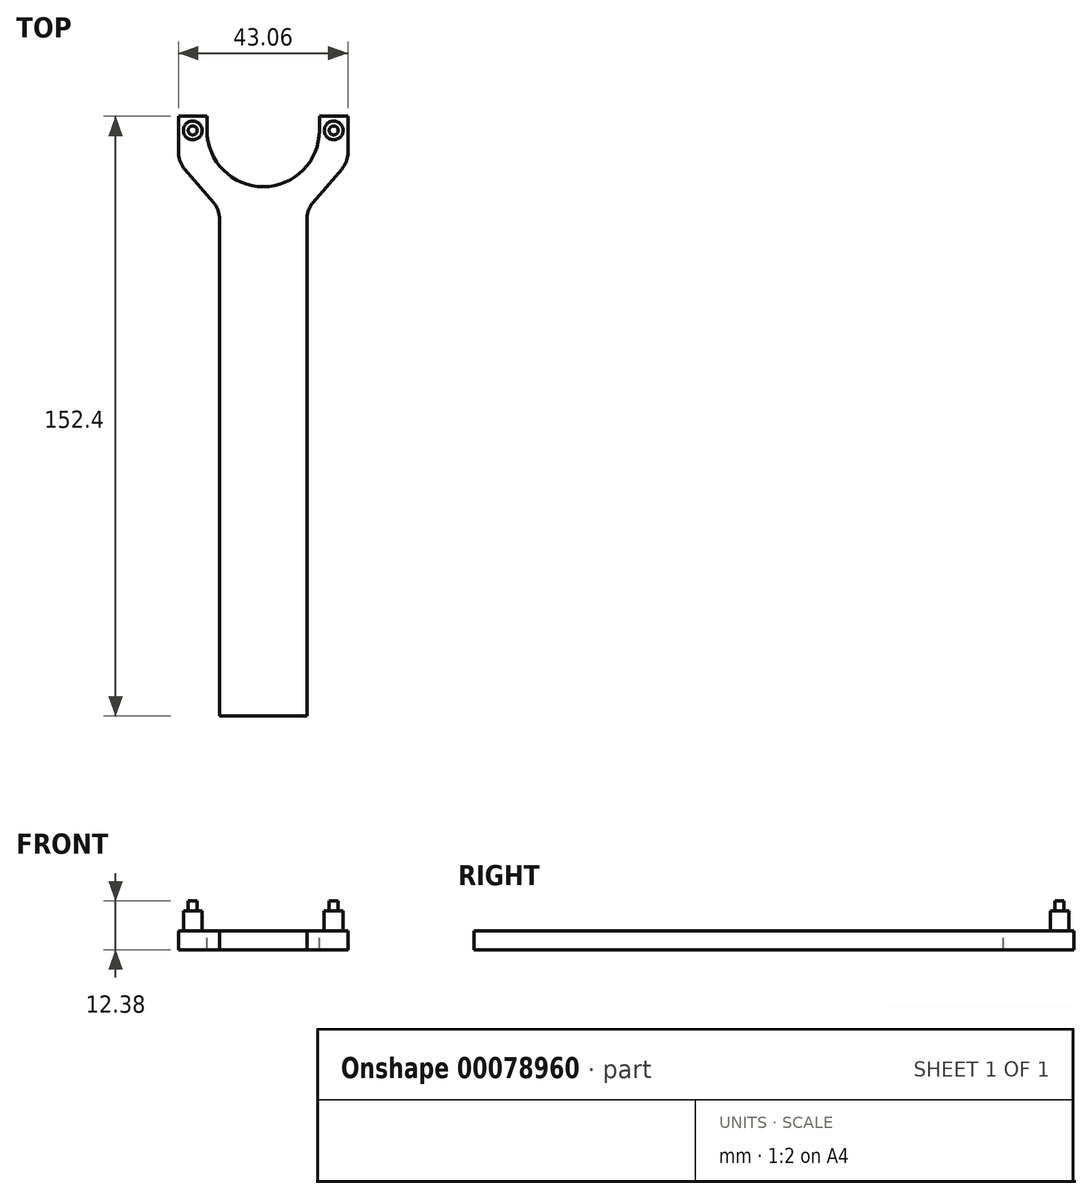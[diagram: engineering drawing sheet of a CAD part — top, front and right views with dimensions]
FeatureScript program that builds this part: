
annotation { "Feature Type Name" : "Feature", "Feature Type Description" : "" }
export const myFeature = defineFeature(function(context is Context, id is Id, definition is map)
    precondition{}
    {
        {
            var Q0;
            Q0=qCreatedBy(makeId("Top.planeOp"),FACE);
            var sketch = newSketch(context, id + "F0", { "sketchPlane" : qUnion([Q0])});
            skLineSegment(sketch, "E0.rect.bottom", {"start": v(21.53, 76.2) * mm, "end": v(14.29, 76.2) * mm});
            skLineSegment(sketch, "E0.rect.left", {"start": v(21.53, 76.2) * mm, "end": v(21.53, 64.6) * mm});
            skLineSegment(sketch, "E0.rect.right", {"start": v(-21.53, 76.2) * mm, "end": v(-21.53, 64.6) * mm});
            skPoint(sketch, "E0.rect.middle", {"position": v(0, 0) * mm});
            skCircle(sketch, "E1", {"center": v(17.9, 72.58) * mm, "radius": 2.38 * mm});
            skCircle(sketch, "E2", {"center": v(-17.9, 72.58) * mm, "radius": 2.38 * mm});
            skLineSegment(sketch, "E3", {"start": v(17.9, 72.58) * mm, "end": v(21.53, 72.58) * mm, "construction": true});
            skLineSegment(sketch, "E4", {"start": v(-17.9, 72.58) * mm, "end": v(-21.53, 72.58) * mm, "construction": true});
            skLineSegment(sketch, "E5", {"start": v(17.9, 72.58) * mm, "end": v(17.9, 76.2) * mm, "construction": true});
            skArc(sketch, "E6", {"start": v(-14.29, 72.58) * mm, "mid": v(0, 58.3) * mm, "end": v(14.29, 72.58) * mm});
            skLineSegment(sketch, "E7", {"start": v(-14.29, 72.58) * mm, "end": v(-14.29, 76.2) * mm});
            skLineSegment(sketch, "E8", {"start": v(14.29, 72.58) * mm, "end": v(14.29, 76.2) * mm});
            skLineSegment(sketch, "E9.trimOffspring", {"start": v(-14.29, 76.2) * mm, "end": v(-21.53, 76.2) * mm});
            skLineSegment(sketch, "E10", {"start": v(17.9, 72.58) * mm, "end": v(14.29, 72.58) * mm, "construction": true});
            skLineSegment(sketch, "E11", {"start": v(-17.9, 72.58) * mm, "end": v(-14.29, 72.58) * mm, "construction": true});
            skLineSegment(sketch, "E12.rect.left", {"start": v(14.29, 76.2) * mm, "end": v(14.29, 72.58) * mm});
            skLineSegment(sketch, "E12.rect.right", {"start": v(-14.29, 76.2) * mm, "end": v(-14.29, 72.58) * mm});
            skCircle(sketch, "E13", {"center": v(0, 72.58) * mm, "radius": 21.53 * mm, "construction": true});
            skLineSegment(sketch, "E14", {"start": v(0, 58.3) * mm, "end": v(0, 51.05) * mm, "construction": true});
            skLineSegment(sketch, "E15", {"start": v(21.53, 64.6) * mm, "end": v(11.11, 52.49) * mm});
            skPoint(sketch, "E16", {"position": v(16.32, 58.54) * mm});
            skLineSegment(sketch, "E17", {"start": v(-21.53, 64.6) * mm, "end": v(-11.11, 52.49) * mm});
            skPoint(sketch, "E18.orphan", {"position": v(-21.53, -76.2) * mm});
            skPoint(sketch, "E19.orphan", {"position": v(21.53, -76.2) * mm});
            skLineSegment(sketch, "E20", {"start": v(-11.11, 52.49) * mm, "end": v(-11.11, -76.2) * mm});
            skLineSegment(sketch, "E21", {"start": v(-11.11, -76.2) * mm, "end": v(11.11, -76.2) * mm});
            skLineSegment(sketch, "E22", {"start": v(11.11, -76.2) * mm, "end": v(11.11, 52.49) * mm});
            skPoint(sketch, "E23", {"position": v(-16.32, 58.54) * mm});
            skCircle(sketch, "E24", {"center": v(-17.9, 72.58) * mm, "radius": 1.14 * mm});
            skCircle(sketch, "E25", {"center": v(17.9, 72.58) * mm, "radius": 1.14 * mm});
            skSolve(sketch);
        }
        {
            var Q0;
            Q0=makeQuery(id+"F0.imprint","IMPRINT",FACE,{"disambiguationData":[TD([[makeQuery(id+"F0.imprint","IMPRINT",EDGE,{"derivedFrom":sQuery(id+"F0.wireOp",EDGE,"E0.rect.bottom")}),1.0]])]});
            var Q1;
            Q1=makeQuery(id+"F0.imprint","IMPRINT",FACE,{"disambiguationData":[TD([[makeQuery(id+"F0.imprint","IMPRINT",EDGE,{"derivedFrom":sQuery(id+"F0.wireOp",EDGE,"E2")}),1.0]])]});
            var Q2;
            Q2=makeQuery(id+"F0.imprint","IMPRINT",FACE,{"disambiguationData":[TD([[makeQuery(id+"F0.imprint","IMPRINT",EDGE,{"derivedFrom":sQuery(id+"F0.wireOp",EDGE,"E1")}),1.0]])]});
            var Q3;
            Q3=makeQuery(id+"F0.imprint","IMPRINT",FACE,{"disambiguationData":[TD([[makeQuery(id+"F0.imprint","IMPRINT",EDGE,{"derivedFrom":sQuery(id+"F0.wireOp",EDGE,"E24")}),1.0]])]});
            var Q4;
            Q4=makeQuery(id+"F0.imprint","IMPRINT",FACE,{"disambiguationData":[TD([[makeQuery(id+"F0.imprint","IMPRINT",EDGE,{"derivedFrom":sQuery(id+"F0.wireOp",EDGE,"E25")}),1.0]])]});
            extrude(context, id + "F1", {"entities" : qUnion([Q0, Q1, Q2, Q3, Q4]), "oppositeDirection" : true, "depth" : 4.76 * mm});
        }
        {
            var Q0;
            Q0=makeQuery(id+"F1.opExtrude","SWEPT_EDGE",EDGE,{"disambiguationData":[OSD([sQuery(id+"F0.wireOp",EDGE,"E0.rect.left"),sQuery(id+"F0.wireOp",EDGE,"E15")])]});
            var Q1;
            Q1=makeQuery(id+"F1.opExtrude","SWEPT_EDGE",EDGE,{"disambiguationData":[OSD([sQuery(id+"F0.wireOp",EDGE,"E15"),sQuery(id+"F0.wireOp",EDGE,"E22")])]});
            var Q2;
            Q2=makeQuery(id+"F1.opExtrude","SWEPT_EDGE",EDGE,{"disambiguationData":[OSD([sQuery(id+"F0.wireOp",EDGE,"E0.rect.right"),sQuery(id+"F0.wireOp",EDGE,"E17")])]});
            var Q3;
            Q3=makeQuery(id+"F1.opExtrude","SWEPT_EDGE",EDGE,{"disambiguationData":[OSD([sQuery(id+"F0.wireOp",EDGE,"E17"),sQuery(id+"F0.wireOp",EDGE,"E20")])]});
            fillet(context, id + "F2", {"entities" : qUnion([Q0, Q1, Q2, Q3]), "radius" : 6.35 * mm, "tangentPropagation" : true, "allowEdgeOverflow" : false});
        }
        {
            var Q0;
            Q0=makeQuery(id+"F0.imprint","IMPRINT",FACE,{"disambiguationData":[TD([[makeQuery(id+"F0.imprint","IMPRINT",EDGE,{"derivedFrom":sQuery(id+"F0.wireOp",EDGE,"E25")}),1.0]])]});
            var Q1;
            Q1=makeQuery(id+"F0.imprint","IMPRINT",FACE,{"disambiguationData":[TD([[makeQuery(id+"F0.imprint","IMPRINT",EDGE,{"derivedFrom":sQuery(id+"F0.wireOp",EDGE,"E24")}),1.0]])]});
            extrude(context, id + "F3", {"entities" : qUnion([Q0, Q1]), "operationType" : NewBodyOperationType.ADD, "depth" : 7.62 * mm});
        }
        {
            var Q0;
            Q0=makeQuery(id+"F0.imprint","IMPRINT",FACE,{"disambiguationData":[TD([[makeQuery(id+"F0.imprint","IMPRINT",EDGE,{"derivedFrom":sQuery(id+"F0.wireOp",EDGE,"E2")}),1.0]])]});
            var Q1;
            Q1=makeQuery(id+"F0.imprint","IMPRINT",FACE,{"disambiguationData":[TD([[makeQuery(id+"F0.imprint","IMPRINT",EDGE,{"derivedFrom":sQuery(id+"F0.wireOp",EDGE,"E1")}),1.0]])]});
            extrude(context, id + "F4", {"entities" : qUnion([Q0, Q1]), "operationType" : NewBodyOperationType.ADD, "depth" : 5.08 * mm});
        }
    });
